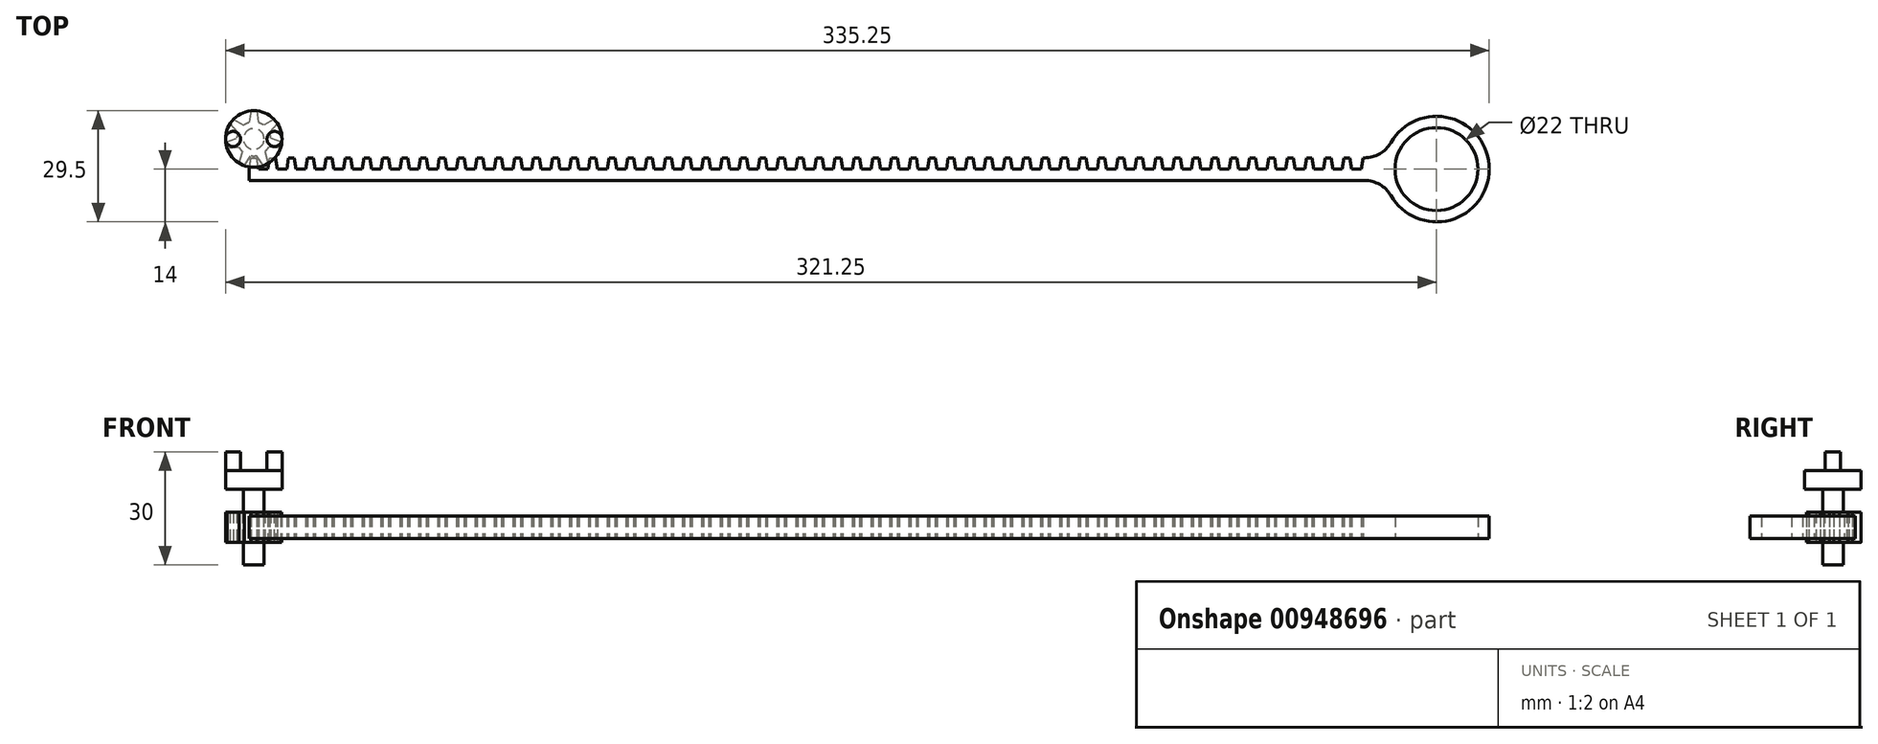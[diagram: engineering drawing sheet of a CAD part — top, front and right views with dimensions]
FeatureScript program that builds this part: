
annotation { "Feature Type Name" : "Feature", "Feature Type Description" : "" }
export const myFeature = defineFeature(function(context is Context, id is Id, definition is map)
    precondition{}
    {
        {
            var Q0;
            Q0=qCreatedBy(makeId("Top.planeOp"),FACE);
            var sketch = newSketch(context, id + "F0", { "sketchPlane" : qUnion([Q0])});
            skArc(sketch, "E0", {"start": v(6.3, 4.07) * mm, "mid": v(5.86, 4.68) * mm, "end": v(5.37, 5.24) * mm});
            skArc(sketch, "E1.0", {"start": v(2.6, 3.67) * mm, "mid": v(1.95, 4.05) * mm, "end": v(1.25, 4.32) * mm});
            skLineSegment(sketch, "E2", {"start": v(-0.75, 7.46) * mm, "end": v(-1.25, 4.32) * mm});
            skLineSegment(sketch, "E3", {"start": v(0, 7.5) * mm, "end": v(0, 4.5) * mm, "construction": true});
            skLineSegment(sketch, "E4.MirrorCS", {"start": v(0.75, 7.46) * mm, "end": v(1.25, 4.32) * mm});
            skLineSegment(sketch, "E5.1.0", {"start": v(-5.37, 5.24) * mm, "end": v(-2.6, 3.67) * mm});
            skLineSegment(sketch, "E5.1.1", {"start": v(-6.3, 4.07) * mm, "end": v(-4.16, 1.72) * mm});
            skLineSegment(sketch, "E5.2.0", {"start": v(-7.44, -0.93) * mm, "end": v(-4.5, 0.26) * mm});
            skLineSegment(sketch, "E5.2.1", {"start": v(-7.1, -2.4) * mm, "end": v(-3.94, -2.18) * mm});
            skLineSegment(sketch, "E5.3.0", {"start": v(-3.91, -6.4) * mm, "end": v(-3, -3.35) * mm});
            skLineSegment(sketch, "E5.3.1", {"start": v(-2.56, -7.05) * mm, "end": v(-0.75, -4.44) * mm});
            skLineSegment(sketch, "E5.4.0", {"start": v(2.56, -7.05) * mm, "end": v(0.75, -4.44) * mm});
            skLineSegment(sketch, "E5.4.1", {"start": v(3.91, -6.4) * mm, "end": v(3, -3.35) * mm});
            skLineSegment(sketch, "E5.5.0", {"start": v(7.1, -2.4) * mm, "end": v(3.94, -2.18) * mm});
            skLineSegment(sketch, "E5.5.1", {"start": v(7.44, -0.93) * mm, "end": v(4.5, 0.26) * mm});
            skLineSegment(sketch, "E5.6.0", {"start": v(6.3, 4.07) * mm, "end": v(4.16, 1.72) * mm});
            skLineSegment(sketch, "E5.6.1", {"start": v(5.37, 5.24) * mm, "end": v(2.6, 3.67) * mm});
            skLineSegment(sketch, "E6", {"start": v(0, 0) * mm, "end": v(0, -14.56) * mm, "construction": true});
            skLineSegment(sketch, "E7", {"start": v(-1.25, -8) * mm, "end": v(-0.75, -5) * mm});
            skLineSegment(sketch, "E8.MirrorCS", {"start": v(1.25, -8) * mm, "end": v(0.75, -5) * mm});
            skLineSegment(sketch, "E9", {"start": v(-0.75, -5) * mm, "end": v(0.75, -5) * mm});
            skLineSegment(sketch, "E10", {"start": v(1.25, -8) * mm, "end": v(3.75, -8) * mm});
            skLineSegment(sketch, "E11.1.0.0", {"start": v(6.25, -8) * mm, "end": v(8.75, -8) * mm});
            skLineSegment(sketch, "E11.1.0.1", {"start": v(6.25, -8) * mm, "end": v(5.75, -5) * mm});
            skLineSegment(sketch, "E11.1.0.2", {"start": v(4.25, -5) * mm, "end": v(5.75, -5) * mm});
            skLineSegment(sketch, "E11.1.0.3", {"start": v(3.75, -8) * mm, "end": v(4.25, -5) * mm});
            skLineSegment(sketch, "E11.2.0.0", {"start": v(11.25, -8) * mm, "end": v(13.75, -8) * mm});
            skLineSegment(sketch, "E11.2.0.1", {"start": v(11.25, -8) * mm, "end": v(10.75, -5) * mm});
            skLineSegment(sketch, "E11.2.0.2", {"start": v(9.25, -5) * mm, "end": v(10.75, -5) * mm});
            skLineSegment(sketch, "E11.2.0.3", {"start": v(8.75, -8) * mm, "end": v(9.25, -5) * mm});
            skLineSegment(sketch, "E11.3.0.0", {"start": v(16.25, -8) * mm, "end": v(18.75, -8) * mm});
            skLineSegment(sketch, "E11.3.0.1", {"start": v(16.25, -8) * mm, "end": v(15.75, -5) * mm});
            skLineSegment(sketch, "E11.3.0.2", {"start": v(14.25, -5) * mm, "end": v(15.75, -5) * mm});
            skLineSegment(sketch, "E11.3.0.3", {"start": v(13.75, -8) * mm, "end": v(14.25, -5) * mm});
            skLineSegment(sketch, "E11.4.0.0", {"start": v(21.25, -8) * mm, "end": v(23.75, -8) * mm});
            skLineSegment(sketch, "E11.4.0.1", {"start": v(21.25, -8) * mm, "end": v(20.75, -5) * mm});
            skLineSegment(sketch, "E11.4.0.2", {"start": v(19.25, -5) * mm, "end": v(20.75, -5) * mm});
            skLineSegment(sketch, "E11.4.0.3", {"start": v(18.75, -8) * mm, "end": v(19.25, -5) * mm});
            skLineSegment(sketch, "E11.5.0.0", {"start": v(26.25, -8) * mm, "end": v(28.75, -8) * mm});
            skLineSegment(sketch, "E11.5.0.1", {"start": v(26.25, -8) * mm, "end": v(25.75, -5) * mm});
            skLineSegment(sketch, "E11.5.0.2", {"start": v(24.25, -5) * mm, "end": v(25.75, -5) * mm});
            skLineSegment(sketch, "E11.5.0.3", {"start": v(23.75, -8) * mm, "end": v(24.25, -5) * mm});
            skLineSegment(sketch, "E11.6.0.0", {"start": v(31.25, -8) * mm, "end": v(33.75, -8) * mm});
            skLineSegment(sketch, "E11.6.0.1", {"start": v(31.25, -8) * mm, "end": v(30.75, -5) * mm});
            skLineSegment(sketch, "E11.6.0.2", {"start": v(29.25, -5) * mm, "end": v(30.75, -5) * mm});
            skLineSegment(sketch, "E11.6.0.3", {"start": v(28.75, -8) * mm, "end": v(29.25, -5) * mm});
            skLineSegment(sketch, "E11.7.0.0", {"start": v(36.25, -8) * mm, "end": v(38.75, -8) * mm});
            skLineSegment(sketch, "E11.7.0.1", {"start": v(36.25, -8) * mm, "end": v(35.75, -5) * mm});
            skLineSegment(sketch, "E11.7.0.2", {"start": v(34.25, -5) * mm, "end": v(35.75, -5) * mm});
            skLineSegment(sketch, "E11.7.0.3", {"start": v(33.75, -8) * mm, "end": v(34.25, -5) * mm});
            skLineSegment(sketch, "E11.8.0.0", {"start": v(41.25, -8) * mm, "end": v(43.75, -8) * mm});
            skLineSegment(sketch, "E11.8.0.1", {"start": v(41.25, -8) * mm, "end": v(40.75, -5) * mm});
            skLineSegment(sketch, "E11.8.0.2", {"start": v(39.25, -5) * mm, "end": v(40.75, -5) * mm});
            skLineSegment(sketch, "E11.8.0.3", {"start": v(38.75, -8) * mm, "end": v(39.25, -5) * mm});
            skLineSegment(sketch, "E11.9.0.0", {"start": v(46.25, -8) * mm, "end": v(48.75, -8) * mm});
            skLineSegment(sketch, "E11.9.0.1", {"start": v(46.25, -8) * mm, "end": v(45.75, -5) * mm});
            skLineSegment(sketch, "E11.9.0.2", {"start": v(44.25, -5) * mm, "end": v(45.75, -5) * mm});
            skLineSegment(sketch, "E11.9.0.3", {"start": v(43.75, -8) * mm, "end": v(44.25, -5) * mm});
            skLineSegment(sketch, "E11.10.0.0", {"start": v(51.25, -8) * mm, "end": v(53.75, -8) * mm});
            skLineSegment(sketch, "E11.10.0.1", {"start": v(51.25, -8) * mm, "end": v(50.75, -5) * mm});
            skLineSegment(sketch, "E11.10.0.2", {"start": v(49.25, -5) * mm, "end": v(50.75, -5) * mm});
            skLineSegment(sketch, "E11.10.0.3", {"start": v(48.75, -8) * mm, "end": v(49.25, -5) * mm});
            skLineSegment(sketch, "E11.11.0.0", {"start": v(56.25, -8) * mm, "end": v(58.75, -8) * mm});
            skLineSegment(sketch, "E11.11.0.1", {"start": v(56.25, -8) * mm, "end": v(55.75, -5) * mm});
            skLineSegment(sketch, "E11.11.0.2", {"start": v(54.25, -5) * mm, "end": v(55.75, -5) * mm});
            skLineSegment(sketch, "E11.11.0.3", {"start": v(53.75, -8) * mm, "end": v(54.25, -5) * mm});
            skLineSegment(sketch, "E11.12.0.0", {"start": v(61.25, -8) * mm, "end": v(63.75, -8) * mm});
            skLineSegment(sketch, "E11.12.0.1", {"start": v(61.25, -8) * mm, "end": v(60.75, -5) * mm});
            skLineSegment(sketch, "E11.12.0.2", {"start": v(59.25, -5) * mm, "end": v(60.75, -5) * mm});
            skLineSegment(sketch, "E11.12.0.3", {"start": v(58.75, -8) * mm, "end": v(59.25, -5) * mm});
            skLineSegment(sketch, "E11.13.0.0", {"start": v(66.25, -8) * mm, "end": v(68.75, -8) * mm});
            skLineSegment(sketch, "E11.13.0.1", {"start": v(66.25, -8) * mm, "end": v(65.75, -5) * mm});
            skLineSegment(sketch, "E11.13.0.2", {"start": v(64.25, -5) * mm, "end": v(65.75, -5) * mm});
            skLineSegment(sketch, "E11.13.0.3", {"start": v(63.75, -8) * mm, "end": v(64.25, -5) * mm});
            skLineSegment(sketch, "E11.14.0.0", {"start": v(71.25, -8) * mm, "end": v(73.75, -8) * mm});
            skLineSegment(sketch, "E11.14.0.1", {"start": v(71.25, -8) * mm, "end": v(70.75, -5) * mm});
            skLineSegment(sketch, "E11.14.0.2", {"start": v(69.25, -5) * mm, "end": v(70.75, -5) * mm});
            skLineSegment(sketch, "E11.14.0.3", {"start": v(68.75, -8) * mm, "end": v(69.25, -5) * mm});
            skLineSegment(sketch, "E11.15.0.0", {"start": v(76.25, -8) * mm, "end": v(78.75, -8) * mm});
            skLineSegment(sketch, "E11.15.0.1", {"start": v(76.25, -8) * mm, "end": v(75.75, -5) * mm});
            skLineSegment(sketch, "E11.15.0.2", {"start": v(74.25, -5) * mm, "end": v(75.75, -5) * mm});
            skLineSegment(sketch, "E11.15.0.3", {"start": v(73.75, -8) * mm, "end": v(74.25, -5) * mm});
            skLineSegment(sketch, "E11.16.0.0", {"start": v(81.25, -8) * mm, "end": v(83.75, -8) * mm});
            skLineSegment(sketch, "E11.16.0.1", {"start": v(81.25, -8) * mm, "end": v(80.75, -5) * mm});
            skLineSegment(sketch, "E11.16.0.2", {"start": v(79.25, -5) * mm, "end": v(80.75, -5) * mm});
            skLineSegment(sketch, "E11.16.0.3", {"start": v(78.75, -8) * mm, "end": v(79.25, -5) * mm});
            skLineSegment(sketch, "E11.17.0.0", {"start": v(86.25, -8) * mm, "end": v(88.75, -8) * mm});
            skLineSegment(sketch, "E11.17.0.1", {"start": v(86.25, -8) * mm, "end": v(85.75, -5) * mm});
            skLineSegment(sketch, "E11.17.0.2", {"start": v(84.25, -5) * mm, "end": v(85.75, -5) * mm});
            skLineSegment(sketch, "E11.17.0.3", {"start": v(83.75, -8) * mm, "end": v(84.25, -5) * mm});
            skLineSegment(sketch, "E11.18.0.0", {"start": v(91.25, -8) * mm, "end": v(93.75, -8) * mm});
            skLineSegment(sketch, "E11.18.0.1", {"start": v(91.25, -8) * mm, "end": v(90.75, -5) * mm});
            skLineSegment(sketch, "E11.18.0.2", {"start": v(89.25, -5) * mm, "end": v(90.75, -5) * mm});
            skLineSegment(sketch, "E11.18.0.3", {"start": v(88.75, -8) * mm, "end": v(89.25, -5) * mm});
            skLineSegment(sketch, "E11.19.0.0", {"start": v(96.25, -8) * mm, "end": v(98.75, -8) * mm});
            skLineSegment(sketch, "E11.19.0.1", {"start": v(96.25, -8) * mm, "end": v(95.75, -5) * mm});
            skLineSegment(sketch, "E11.19.0.2", {"start": v(94.25, -5) * mm, "end": v(95.75, -5) * mm});
            skLineSegment(sketch, "E11.19.0.3", {"start": v(93.75, -8) * mm, "end": v(94.25, -5) * mm});
            skLineSegment(sketch, "E11.direction1", {"start": v(1.25, -8) * mm, "end": v(6.25, -8) * mm, "construction": true});
            skArc(sketch, "E12.trimOffspring", {"start": v(0.75, 7.46) * mm, "mid": v(0, 7.5) * mm, "end": v(-0.75, 7.46) * mm});
            skArc(sketch, "E13.trimOffspring", {"start": v(-1.25, 4.32) * mm, "mid": v(-1.95, 4.05) * mm, "end": v(-2.6, 3.67) * mm});
            skArc(sketch, "E14.trimOffspring", {"start": v(-5.37, 5.24) * mm, "mid": v(-5.86, 4.68) * mm, "end": v(-6.3, 4.07) * mm});
            skArc(sketch, "E15.trimOffspring", {"start": v(-4.16, 1.72) * mm, "mid": v(-4.39, 1) * mm, "end": v(-4.5, 0.26) * mm});
            skArc(sketch, "E16.trimOffspring", {"start": v(-7.44, -0.93) * mm, "mid": v(-7.31, -1.67) * mm, "end": v(-7.1, -2.4) * mm});
            skArc(sketch, "E17.trimOffspring", {"start": v(-3.94, -2.18) * mm, "mid": v(-3.52, -2.8) * mm, "end": v(-3, -3.35) * mm});
            skArc(sketch, "E18.trimOffspring", {"start": v(-3.91, -6.4) * mm, "mid": v(-3.25, -6.76) * mm, "end": v(-2.56, -7.05) * mm});
            skArc(sketch, "E19.trimOffspring", {"start": v(-0.75, -4.44) * mm, "mid": v(0, -4.5) * mm, "end": v(0.75, -4.44) * mm});
            skArc(sketch, "E20.trimOffspring", {"start": v(2.56, -7.05) * mm, "mid": v(3.32, -6.73) * mm, "end": v(4.03, -6.33) * mm});
            skArc(sketch, "E21.trimOffspring", {"start": v(3, -3.35) * mm, "mid": v(3.52, -2.8) * mm, "end": v(3.94, -2.18) * mm});
            skArc(sketch, "E22.trimOffspring", {"start": v(7.1, -2.4) * mm, "mid": v(7.31, -1.67) * mm, "end": v(7.44, -0.93) * mm});
            skArc(sketch, "E23.trimOffspring", {"start": v(4.5, 0.26) * mm, "mid": v(4.39, 1) * mm, "end": v(4.16, 1.72) * mm});
            skLineSegment(sketch, "E24.0.20.0", {"start": v(101.25, -8) * mm, "end": v(103.75, -8) * mm});
            skLineSegment(sketch, "E24.3.20.0", {"start": v(101.25, -8) * mm, "end": v(100.75, -5) * mm});
            skLineSegment(sketch, "E24.6.20.0", {"start": v(99.25, -5) * mm, "end": v(100.75, -5) * mm});
            skLineSegment(sketch, "E24.9.20.0", {"start": v(98.75, -8) * mm, "end": v(99.25, -5) * mm});
            skLineSegment(sketch, "E24.0.21.0", {"start": v(106.25, -8) * mm, "end": v(108.75, -8) * mm});
            skLineSegment(sketch, "E24.3.21.0", {"start": v(106.25, -8) * mm, "end": v(105.75, -5) * mm});
            skLineSegment(sketch, "E24.6.21.0", {"start": v(104.25, -5) * mm, "end": v(105.75, -5) * mm});
            skLineSegment(sketch, "E24.9.21.0", {"start": v(103.75, -8) * mm, "end": v(104.25, -5) * mm});
            skLineSegment(sketch, "E24.0.22.0", {"start": v(111.25, -8) * mm, "end": v(113.75, -8) * mm});
            skLineSegment(sketch, "E24.3.22.0", {"start": v(111.25, -8) * mm, "end": v(110.75, -5) * mm});
            skLineSegment(sketch, "E24.6.22.0", {"start": v(109.25, -5) * mm, "end": v(110.75, -5) * mm});
            skLineSegment(sketch, "E24.9.22.0", {"start": v(108.75, -8) * mm, "end": v(109.25, -5) * mm});
            skLineSegment(sketch, "E24.0.23.0", {"start": v(116.25, -8) * mm, "end": v(118.75, -8) * mm});
            skLineSegment(sketch, "E24.3.23.0", {"start": v(116.25, -8) * mm, "end": v(115.75, -5) * mm});
            skLineSegment(sketch, "E24.6.23.0", {"start": v(114.25, -5) * mm, "end": v(115.75, -5) * mm});
            skLineSegment(sketch, "E24.9.23.0", {"start": v(113.75, -8) * mm, "end": v(114.25, -5) * mm});
            skLineSegment(sketch, "E24.0.24.0", {"start": v(121.25, -8) * mm, "end": v(123.75, -8) * mm});
            skLineSegment(sketch, "E24.3.24.0", {"start": v(121.25, -8) * mm, "end": v(120.75, -5) * mm});
            skLineSegment(sketch, "E24.6.24.0", {"start": v(119.25, -5) * mm, "end": v(120.75, -5) * mm});
            skLineSegment(sketch, "E24.9.24.0", {"start": v(118.75, -8) * mm, "end": v(119.25, -5) * mm});
            skLineSegment(sketch, "E24.0.25.0", {"start": v(126.25, -8) * mm, "end": v(128.75, -8) * mm});
            skLineSegment(sketch, "E24.3.25.0", {"start": v(126.25, -8) * mm, "end": v(125.75, -5) * mm});
            skLineSegment(sketch, "E24.6.25.0", {"start": v(124.25, -5) * mm, "end": v(125.75, -5) * mm});
            skLineSegment(sketch, "E24.9.25.0", {"start": v(123.75, -8) * mm, "end": v(124.25, -5) * mm});
            skLineSegment(sketch, "E24.0.26.0", {"start": v(131.25, -8) * mm, "end": v(133.75, -8) * mm});
            skLineSegment(sketch, "E24.3.26.0", {"start": v(131.25, -8) * mm, "end": v(130.75, -5) * mm});
            skLineSegment(sketch, "E24.6.26.0", {"start": v(129.25, -5) * mm, "end": v(130.75, -5) * mm});
            skLineSegment(sketch, "E24.9.26.0", {"start": v(128.75, -8) * mm, "end": v(129.25, -5) * mm});
            skLineSegment(sketch, "E24.0.27.0", {"start": v(136.25, -8) * mm, "end": v(138.75, -8) * mm});
            skLineSegment(sketch, "E24.3.27.0", {"start": v(136.25, -8) * mm, "end": v(135.75, -5) * mm});
            skLineSegment(sketch, "E24.6.27.0", {"start": v(134.25, -5) * mm, "end": v(135.75, -5) * mm});
            skLineSegment(sketch, "E24.9.27.0", {"start": v(133.75, -8) * mm, "end": v(134.25, -5) * mm});
            skLineSegment(sketch, "E24.0.28.0", {"start": v(141.25, -8) * mm, "end": v(143.75, -8) * mm});
            skLineSegment(sketch, "E24.3.28.0", {"start": v(141.25, -8) * mm, "end": v(140.75, -5) * mm});
            skLineSegment(sketch, "E24.6.28.0", {"start": v(139.25, -5) * mm, "end": v(140.75, -5) * mm});
            skLineSegment(sketch, "E24.9.28.0", {"start": v(138.75, -8) * mm, "end": v(139.25, -5) * mm});
            skLineSegment(sketch, "E24.0.29.0", {"start": v(146.25, -8) * mm, "end": v(148.75, -8) * mm});
            skLineSegment(sketch, "E24.3.29.0", {"start": v(146.25, -8) * mm, "end": v(145.75, -5) * mm});
            skLineSegment(sketch, "E24.6.29.0", {"start": v(144.25, -5) * mm, "end": v(145.75, -5) * mm});
            skLineSegment(sketch, "E24.9.29.0", {"start": v(143.75, -8) * mm, "end": v(144.25, -5) * mm});
            skLineSegment(sketch, "E24.0.30.0", {"start": v(151.25, -8) * mm, "end": v(153.75, -8) * mm});
            skLineSegment(sketch, "E24.3.30.0", {"start": v(151.25, -8) * mm, "end": v(150.75, -5) * mm});
            skLineSegment(sketch, "E24.6.30.0", {"start": v(149.25, -5) * mm, "end": v(150.75, -5) * mm});
            skLineSegment(sketch, "E24.9.30.0", {"start": v(148.75, -8) * mm, "end": v(149.25, -5) * mm});
            skLineSegment(sketch, "E24.0.31.0", {"start": v(156.25, -8) * mm, "end": v(158.75, -8) * mm});
            skLineSegment(sketch, "E24.3.31.0", {"start": v(156.25, -8) * mm, "end": v(155.75, -5) * mm});
            skLineSegment(sketch, "E24.6.31.0", {"start": v(154.25, -5) * mm, "end": v(155.75, -5) * mm});
            skLineSegment(sketch, "E24.9.31.0", {"start": v(153.75, -8) * mm, "end": v(154.25, -5) * mm});
            skLineSegment(sketch, "E24.0.32.0", {"start": v(161.25, -8) * mm, "end": v(163.75, -8) * mm});
            skLineSegment(sketch, "E24.3.32.0", {"start": v(161.25, -8) * mm, "end": v(160.75, -5) * mm});
            skLineSegment(sketch, "E24.6.32.0", {"start": v(159.25, -5) * mm, "end": v(160.75, -5) * mm});
            skLineSegment(sketch, "E24.9.32.0", {"start": v(158.75, -8) * mm, "end": v(159.25, -5) * mm});
            skLineSegment(sketch, "E24.0.33.0", {"start": v(166.25, -8) * mm, "end": v(168.75, -8) * mm});
            skLineSegment(sketch, "E24.3.33.0", {"start": v(166.25, -8) * mm, "end": v(165.75, -5) * mm});
            skLineSegment(sketch, "E24.6.33.0", {"start": v(164.25, -5) * mm, "end": v(165.75, -5) * mm});
            skLineSegment(sketch, "E24.9.33.0", {"start": v(163.75, -8) * mm, "end": v(164.25, -5) * mm});
            skLineSegment(sketch, "E24.0.34.0", {"start": v(171.25, -8) * mm, "end": v(173.75, -8) * mm});
            skLineSegment(sketch, "E24.3.34.0", {"start": v(171.25, -8) * mm, "end": v(170.75, -5) * mm});
            skLineSegment(sketch, "E24.6.34.0", {"start": v(169.25, -5) * mm, "end": v(170.75, -5) * mm});
            skLineSegment(sketch, "E24.9.34.0", {"start": v(168.75, -8) * mm, "end": v(169.25, -5) * mm});
            skLineSegment(sketch, "E24.0.35.0", {"start": v(176.25, -8) * mm, "end": v(178.75, -8) * mm});
            skLineSegment(sketch, "E24.3.35.0", {"start": v(176.25, -8) * mm, "end": v(175.75, -5) * mm});
            skLineSegment(sketch, "E24.6.35.0", {"start": v(174.25, -5) * mm, "end": v(175.75, -5) * mm});
            skLineSegment(sketch, "E24.9.35.0", {"start": v(173.75, -8) * mm, "end": v(174.25, -5) * mm});
            skLineSegment(sketch, "E24.0.36.0", {"start": v(181.25, -8) * mm, "end": v(183.75, -8) * mm});
            skLineSegment(sketch, "E24.3.36.0", {"start": v(181.25, -8) * mm, "end": v(180.75, -5) * mm});
            skLineSegment(sketch, "E24.6.36.0", {"start": v(179.25, -5) * mm, "end": v(180.75, -5) * mm});
            skLineSegment(sketch, "E24.9.36.0", {"start": v(178.75, -8) * mm, "end": v(179.25, -5) * mm});
            skLineSegment(sketch, "E24.0.37.0", {"start": v(186.25, -8) * mm, "end": v(188.75, -8) * mm});
            skLineSegment(sketch, "E24.3.37.0", {"start": v(186.25, -8) * mm, "end": v(185.75, -5) * mm});
            skLineSegment(sketch, "E24.6.37.0", {"start": v(184.25, -5) * mm, "end": v(185.75, -5) * mm});
            skLineSegment(sketch, "E24.9.37.0", {"start": v(183.75, -8) * mm, "end": v(184.25, -5) * mm});
            skLineSegment(sketch, "E24.0.38.0", {"start": v(191.25, -8) * mm, "end": v(193.75, -8) * mm});
            skLineSegment(sketch, "E24.3.38.0", {"start": v(191.25, -8) * mm, "end": v(190.75, -5) * mm});
            skLineSegment(sketch, "E24.6.38.0", {"start": v(189.25, -5) * mm, "end": v(190.75, -5) * mm});
            skLineSegment(sketch, "E24.9.38.0", {"start": v(188.75, -8) * mm, "end": v(189.25, -5) * mm});
            skLineSegment(sketch, "E24.0.39.0", {"start": v(196.25, -8) * mm, "end": v(198.75, -8) * mm});
            skLineSegment(sketch, "E24.3.39.0", {"start": v(196.25, -8) * mm, "end": v(195.75, -5) * mm});
            skLineSegment(sketch, "E24.6.39.0", {"start": v(194.25, -5) * mm, "end": v(195.75, -5) * mm});
            skLineSegment(sketch, "E24.9.39.0", {"start": v(193.75, -8) * mm, "end": v(194.25, -5) * mm});
            skLineSegment(sketch, "E24.0.40.0", {"start": v(201.25, -8) * mm, "end": v(203.75, -8) * mm});
            skLineSegment(sketch, "E24.3.40.0", {"start": v(201.25, -8) * mm, "end": v(200.75, -5) * mm});
            skLineSegment(sketch, "E24.6.40.0", {"start": v(199.25, -5) * mm, "end": v(200.75, -5) * mm});
            skLineSegment(sketch, "E24.9.40.0", {"start": v(198.75, -8) * mm, "end": v(199.25, -5) * mm});
            skLineSegment(sketch, "E24.0.41.0", {"start": v(206.25, -8) * mm, "end": v(208.75, -8) * mm});
            skLineSegment(sketch, "E24.3.41.0", {"start": v(206.25, -8) * mm, "end": v(205.75, -5) * mm});
            skLineSegment(sketch, "E24.6.41.0", {"start": v(204.25, -5) * mm, "end": v(205.75, -5) * mm});
            skLineSegment(sketch, "E24.9.41.0", {"start": v(203.75, -8) * mm, "end": v(204.25, -5) * mm});
            skLineSegment(sketch, "E24.0.42.0", {"start": v(211.25, -8) * mm, "end": v(213.75, -8) * mm});
            skLineSegment(sketch, "E24.3.42.0", {"start": v(211.25, -8) * mm, "end": v(210.75, -5) * mm});
            skLineSegment(sketch, "E24.6.42.0", {"start": v(209.25, -5) * mm, "end": v(210.75, -5) * mm});
            skLineSegment(sketch, "E24.9.42.0", {"start": v(208.75, -8) * mm, "end": v(209.25, -5) * mm});
            skLineSegment(sketch, "E24.0.43.0", {"start": v(216.25, -8) * mm, "end": v(218.75, -8) * mm});
            skLineSegment(sketch, "E24.3.43.0", {"start": v(216.25, -8) * mm, "end": v(215.75, -5) * mm});
            skLineSegment(sketch, "E24.6.43.0", {"start": v(214.25, -5) * mm, "end": v(215.75, -5) * mm});
            skLineSegment(sketch, "E24.9.43.0", {"start": v(213.75, -8) * mm, "end": v(214.25, -5) * mm});
            skLineSegment(sketch, "E24.0.44.0", {"start": v(221.25, -8) * mm, "end": v(223.75, -8) * mm});
            skLineSegment(sketch, "E24.3.44.0", {"start": v(221.25, -8) * mm, "end": v(220.75, -5) * mm});
            skLineSegment(sketch, "E24.6.44.0", {"start": v(219.25, -5) * mm, "end": v(220.75, -5) * mm});
            skLineSegment(sketch, "E24.9.44.0", {"start": v(218.75, -8) * mm, "end": v(219.25, -5) * mm});
            skLineSegment(sketch, "E24.0.45.0", {"start": v(226.25, -8) * mm, "end": v(228.75, -8) * mm});
            skLineSegment(sketch, "E24.3.45.0", {"start": v(226.25, -8) * mm, "end": v(225.75, -5) * mm});
            skLineSegment(sketch, "E24.6.45.0", {"start": v(224.25, -5) * mm, "end": v(225.75, -5) * mm});
            skLineSegment(sketch, "E24.9.45.0", {"start": v(223.75, -8) * mm, "end": v(224.25, -5) * mm});
            skLineSegment(sketch, "E24.0.46.0", {"start": v(231.25, -8) * mm, "end": v(233.75, -8) * mm});
            skLineSegment(sketch, "E24.3.46.0", {"start": v(231.25, -8) * mm, "end": v(230.75, -5) * mm});
            skLineSegment(sketch, "E24.6.46.0", {"start": v(229.25, -5) * mm, "end": v(230.75, -5) * mm});
            skLineSegment(sketch, "E24.9.46.0", {"start": v(228.75, -8) * mm, "end": v(229.25, -5) * mm});
            skLineSegment(sketch, "E24.0.47.0", {"start": v(236.25, -8) * mm, "end": v(238.75, -8) * mm});
            skLineSegment(sketch, "E24.3.47.0", {"start": v(236.25, -8) * mm, "end": v(235.75, -5) * mm});
            skLineSegment(sketch, "E24.6.47.0", {"start": v(234.25, -5) * mm, "end": v(235.75, -5) * mm});
            skLineSegment(sketch, "E24.9.47.0", {"start": v(233.75, -8) * mm, "end": v(234.25, -5) * mm});
            skLineSegment(sketch, "E24.0.48.0", {"start": v(241.25, -8) * mm, "end": v(243.75, -8) * mm});
            skLineSegment(sketch, "E24.3.48.0", {"start": v(241.25, -8) * mm, "end": v(240.75, -5) * mm});
            skLineSegment(sketch, "E24.6.48.0", {"start": v(239.25, -5) * mm, "end": v(240.75, -5) * mm});
            skLineSegment(sketch, "E24.9.48.0", {"start": v(238.75, -8) * mm, "end": v(239.25, -5) * mm});
            skLineSegment(sketch, "E24.0.49.0", {"start": v(246.25, -8) * mm, "end": v(248.75, -8) * mm});
            skLineSegment(sketch, "E24.3.49.0", {"start": v(246.25, -8) * mm, "end": v(245.75, -5) * mm});
            skLineSegment(sketch, "E24.6.49.0", {"start": v(244.25, -5) * mm, "end": v(245.75, -5) * mm});
            skLineSegment(sketch, "E24.9.49.0", {"start": v(243.75, -8) * mm, "end": v(244.25, -5) * mm});
            skLineSegment(sketch, "E24.0.50.0", {"start": v(251.25, -8) * mm, "end": v(253.75, -8) * mm});
            skLineSegment(sketch, "E24.3.50.0", {"start": v(251.25, -8) * mm, "end": v(250.75, -5) * mm});
            skLineSegment(sketch, "E24.6.50.0", {"start": v(249.25, -5) * mm, "end": v(250.75, -5) * mm});
            skLineSegment(sketch, "E24.9.50.0", {"start": v(248.75, -8) * mm, "end": v(249.25, -5) * mm});
            skLineSegment(sketch, "E24.0.51.0", {"start": v(256.25, -8) * mm, "end": v(258.75, -8) * mm});
            skLineSegment(sketch, "E24.3.51.0", {"start": v(256.25, -8) * mm, "end": v(255.75, -5) * mm});
            skLineSegment(sketch, "E24.6.51.0", {"start": v(254.25, -5) * mm, "end": v(255.75, -5) * mm});
            skLineSegment(sketch, "E24.9.51.0", {"start": v(253.75, -8) * mm, "end": v(254.25, -5) * mm});
            skLineSegment(sketch, "E24.0.52.0", {"start": v(261.25, -8) * mm, "end": v(263.75, -8) * mm});
            skLineSegment(sketch, "E24.3.52.0", {"start": v(261.25, -8) * mm, "end": v(260.75, -5) * mm});
            skLineSegment(sketch, "E24.6.52.0", {"start": v(259.25, -5) * mm, "end": v(260.75, -5) * mm});
            skLineSegment(sketch, "E24.9.52.0", {"start": v(258.75, -8) * mm, "end": v(259.25, -5) * mm});
            skLineSegment(sketch, "E24.0.53.0", {"start": v(266.25, -8) * mm, "end": v(268.75, -8) * mm});
            skLineSegment(sketch, "E24.3.53.0", {"start": v(266.25, -8) * mm, "end": v(265.75, -5) * mm});
            skLineSegment(sketch, "E24.6.53.0", {"start": v(264.25, -5) * mm, "end": v(265.75, -5) * mm});
            skLineSegment(sketch, "E24.9.53.0", {"start": v(263.75, -8) * mm, "end": v(264.25, -5) * mm});
            skLineSegment(sketch, "E24.0.54.0", {"start": v(271.25, -8) * mm, "end": v(273.75, -8) * mm});
            skLineSegment(sketch, "E24.3.54.0", {"start": v(271.25, -8) * mm, "end": v(270.75, -5) * mm});
            skLineSegment(sketch, "E24.6.54.0", {"start": v(269.25, -5) * mm, "end": v(270.75, -5) * mm});
            skLineSegment(sketch, "E24.9.54.0", {"start": v(268.75, -8) * mm, "end": v(269.25, -5) * mm});
            skLineSegment(sketch, "E24.0.55.0", {"start": v(276.25, -8) * mm, "end": v(278.75, -8) * mm});
            skLineSegment(sketch, "E24.3.55.0", {"start": v(276.25, -8) * mm, "end": v(275.75, -5) * mm});
            skLineSegment(sketch, "E24.6.55.0", {"start": v(274.25, -5) * mm, "end": v(275.75, -5) * mm});
            skLineSegment(sketch, "E24.9.55.0", {"start": v(273.75, -8) * mm, "end": v(274.25, -5) * mm});
            skLineSegment(sketch, "E24.0.56.0", {"start": v(281.25, -8) * mm, "end": v(283.75, -8) * mm});
            skLineSegment(sketch, "E24.3.56.0", {"start": v(281.25, -8) * mm, "end": v(280.75, -5) * mm});
            skLineSegment(sketch, "E24.6.56.0", {"start": v(279.25, -5) * mm, "end": v(280.75, -5) * mm});
            skLineSegment(sketch, "E24.9.56.0", {"start": v(278.75, -8) * mm, "end": v(279.25, -5) * mm});
            skLineSegment(sketch, "E24.0.57.0", {"start": v(286.25, -8) * mm, "end": v(288.75, -8) * mm});
            skLineSegment(sketch, "E24.3.57.0", {"start": v(286.25, -8) * mm, "end": v(285.75, -5) * mm});
            skLineSegment(sketch, "E24.6.57.0", {"start": v(284.25, -5) * mm, "end": v(285.75, -5) * mm});
            skLineSegment(sketch, "E24.9.57.0", {"start": v(283.75, -8) * mm, "end": v(284.25, -5) * mm});
            skLineSegment(sketch, "E24.0.58.0", {"start": v(291.25, -8) * mm, "end": v(293.75, -8) * mm});
            skLineSegment(sketch, "E24.3.58.0", {"start": v(291.25, -8) * mm, "end": v(290.75, -5) * mm});
            skLineSegment(sketch, "E24.6.58.0", {"start": v(289.25, -5) * mm, "end": v(290.75, -5) * mm});
            skLineSegment(sketch, "E24.9.58.0", {"start": v(288.75, -8) * mm, "end": v(289.25, -5) * mm});
            skLineSegment(sketch, "E24.9.59.0", {"start": v(293.75, -8) * mm, "end": v(294.25, -5) * mm});
            skLineSegment(sketch, "E25", {"start": v(-1.25, -11) * mm, "end": v(294.7, -11) * mm});
            skLineSegment(sketch, "E26", {"start": v(-1.25, -8) * mm, "end": v(-1.25, -11) * mm});
            skLineSegment(sketch, "E27", {"start": v(293.75, -8) * mm, "end": v(313.75, -8) * mm, "construction": true});
            skCircle(sketch, "E28", {"center": v(313.75, -8) * mm, "radius": 11 * mm});
            skArc(sketch, "E29", {"start": v(301.63, -15) * mm, "mid": v(327.75, -8) * mm, "end": v(301.63, -1) * mm});
            skArc(sketch, "E30.filletArc", {"start": v(301.63, -15) * mm, "mid": v(298.7, -12.07) * mm, "end": v(294.7, -11) * mm});
            skLineSegment(sketch, "E31", {"start": v(294.25, -5) * mm, "end": v(294.7, -5) * mm});
            skArc(sketch, "E32.filletArc", {"start": v(294.7, -5) * mm, "mid": v(298.7, -3.93) * mm, "end": v(301.63, -1) * mm});
            skCircle(sketch, "E33", {"center": v(0, 0) * mm, "radius": 2.75 * mm});
            skSolve(sketch);
        }
        {
            var Q0;
            Q0=makeQuery(id+"F0.imprint","IMPRINT",FACE,{"disambiguationData":[TD([[makeQuery(id+"F0.imprint","IMPRINT",EDGE,{"derivedFrom":sQuery(id+"F0.wireOp",EDGE,"E0")}),1.0]])]});
            extrude(context, id + "F1", {"entities" : qUnion([Q0]), "endBound" : BoundingType.SYMMETRIC, "depth" : 8 * mm, "offsetDistance" : 25 * mm});
        }
        {
            var Q0;
            Q0=makeQuery(id+"F0.imprint","IMPRINT",FACE,{"disambiguationData":[TD([[makeQuery(id+"F0.imprint","IMPRINT",EDGE,{"derivedFrom":sQuery(id+"F0.wireOp",EDGE,"E7")}),-1.0]])]});
            extrude(context, id + "F2", {"entities" : qUnion([Q0]), "endBound" : BoundingType.SYMMETRIC, "depth" : 6 * mm, "offsetDistance" : 25 * mm});
        }
        {
            var Q0;
            Q0=makeQuery(id+"F0.imprint","IMPRINT",FACE,{"disambiguationData":[TD([[makeQuery(id+"F0.imprint","IMPRINT",EDGE,{"derivedFrom":sQuery(id+"F0.wireOp",EDGE,"E33")}),1.0]])]});
            extrude(context, id + "F3", {"entities" : qUnion([Q0]), "operationType" : NewBodyOperationType.ADD, "endBound" : BoundingType.SYMMETRIC, "depth" : 20 * mm, "offsetDistance" : 25 * mm});
        }
        {
            var Q0;
            Q0=makeQuery(id+"F3.opExtrude","CAP_FACE",FACE,{"disambiguationData":[OSD([sQuery(id+"F0.wireOp",EDGE,"E33")])],"isStart":false});
            var sketch = newSketch(context, id + "F4", { "sketchPlane" : qUnion([Q0])});
            skCircle(sketch, "E34", {"center": v(0, 0) * mm, "radius": 7.5 * mm});
            skSolve(sketch);
        }
        {
            var Q0;
            Q0 = qSketchRegion(id + "F4", true);
            extrude(context, id + "F5", {"entities" : qUnion([Q0]), "operationType" : NewBodyOperationType.ADD, "depth" : 5 * mm, "offsetDistance" : 25 * mm});
        }
        {
            var Q0;
            Q0=makeQuery(id+"F5.opExtrude","CAP_FACE",FACE,{"disambiguationData":[OSD([sQuery(id+"F4.wireOp",EDGE,"E34")])],"isStart":false});
            var sketch = newSketch(context, id + "F6", { "sketchPlane" : qUnion([Q0])});
            skLineSegment(sketch, "E35", {"start": v(-7.5, 0) * mm, "end": v(7.5, 0) * mm, "construction": true});
            skCircle(sketch, "E36", {"center": v(-5.5, 0) * mm, "radius": 2 * mm});
            skCircle(sketch, "E37", {"center": v(5.5, 0) * mm, "radius": 2 * mm});
            skSolve(sketch);
        }
        {
            var Q0;
            Q0 = qSketchRegion(id + "F6", true);
            extrude(context, id + "F7", {"entities" : qUnion([Q0]), "operationType" : NewBodyOperationType.ADD, "depth" : 5 * mm, "offsetDistance" : 25 * mm});
        }
    });
